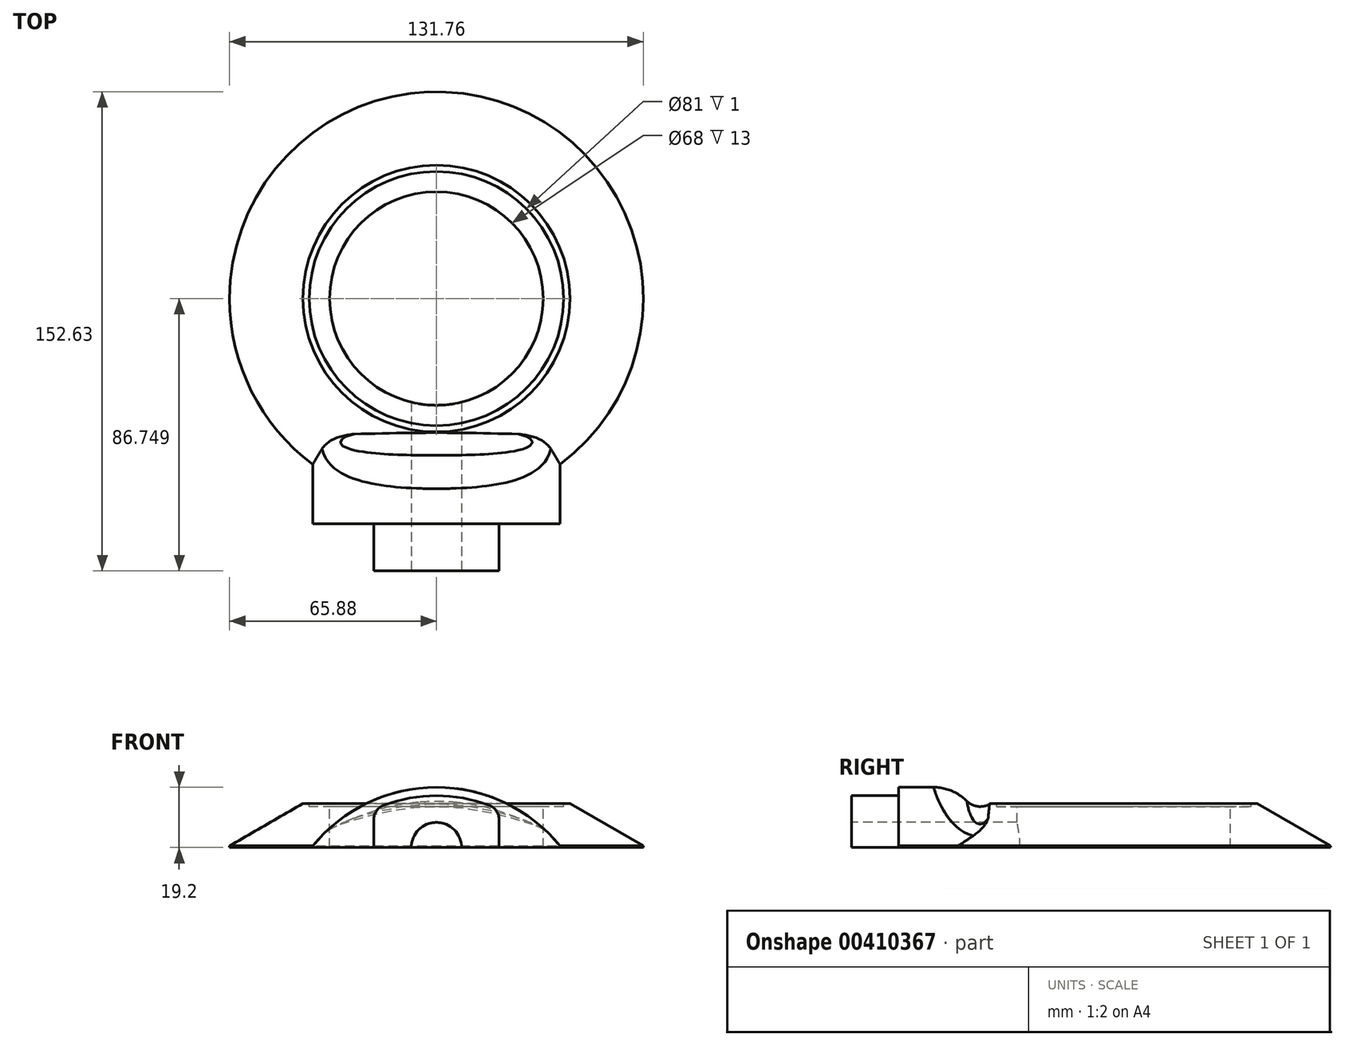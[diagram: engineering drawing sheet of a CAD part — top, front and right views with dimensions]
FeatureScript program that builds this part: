
annotation { "Feature Type Name" : "Feature", "Feature Type Description" : "" }
export const myFeature = defineFeature(function(context is Context, id is Id, definition is map)
    precondition{}
    {
        {
            var Q0;
            Q0=qCreatedBy(makeId("Front.planeOp"),FACE);
            var sketch = newSketch(context, id + "F0", { "sketchPlane" : qUnion([Q0])});
            skLineSegment(sketch, "E0", {"start": v(-39.5, 0) * mm, "end": v(39.5, 0) * mm});
            skPoint(sketch, "E1", {"position": v(0, 19) * mm});
            skLineSegment(sketch, "E2", {"start": v(39.5, 0) * mm, "end": v(39.5, 0) * mm});
            skLineSegment(sketch, "E3.MirrorCS", {"start": v(-39.5, 0) * mm, "end": v(-39.5, 0) * mm});
            skArc(sketch, "E4", {"start": v(39.5, 0) * mm, "mid": v(0, 19) * mm, "end": v(-39.5, 0) * mm});
            skSolve(sketch);
        }
        {
            var Q0;
            Q0=qCreatedBy(makeId("Front.planeOp"),FACE);
            var sketch = newSketch(context, id + "F1", { "sketchPlane" : qUnion([Q0])});
            skLineSegment(sketch, "E5.0", {"start": v(-39.35, 0) * mm, "end": v(0, 0) * mm});
            skArc(sketch, "E6.0", {"start": v(0, 19.2) * mm, "mid": v(-21.79, 14.29) * mm, "end": v(-39.35, 0.5) * mm});
            skLineSegment(sketch, "E7", {"start": v(-39.35, 0.5) * mm, "end": v(-39.35, 0) * mm});
            skArc(sketch, "E8.MirrorCS", {"start": v(0, 19.2) * mm, "mid": v(21.79, 14.29) * mm, "end": v(39.35, 0.5) * mm});
            skLineSegment(sketch, "E9.MirrorCS", {"start": v(39.35, 0.5) * mm, "end": v(39.35, 0) * mm});
            skLineSegment(sketch, "E10.MirrorCS", {"start": v(39.35, 0) * mm, "end": v(0, 0) * mm});
            skSolve(sketch);
        }
        {
            var Q0;
            Q0=qCreatedBy(makeId("Front.planeOp"),FACE);
            var sketch = newSketch(context, id + "F2", { "sketchPlane" : qUnion([Q0])});
            skArc(sketch, "E11.0", {"start": v(20, 12.14) * mm, "mid": v(0, 16.5) * mm, "end": v(-20, 12.14) * mm});
            skLineSegment(sketch, "E12", {"start": v(-20, 0) * mm, "end": v(20, 0) * mm});
            skLineSegment(sketch, "E13", {"start": v(20, 0) * mm, "end": v(20, 12.14) * mm});
            skLineSegment(sketch, "E14.MirrorCS", {"start": v(-20, 0) * mm, "end": v(-20, 12.14) * mm});
            skPoint(sketch, "E15.orphan", {"position": v(-36.25, 0) * mm});
            skSolve(sketch);
        }
        {
            var Q0;
            Q0=qCreatedBy(makeId("Right.planeOp"),FACE);
            var sketch = newSketch(context, id + "F3", { "sketchPlane" : qUnion([Q0])});
            skLineSegment(sketch, "E16", {"start": v(138.5, 0) * mm, "end": v(71.75, 0) * mm, "construction": true});
            skLineSegment(sketch, "E17", {"start": v(5.87, 0.5) * mm, "end": v(29.25, 14) * mm});
            skLineSegment(sketch, "E18", {"start": v(29.25, 14) * mm, "end": v(71.75, 14) * mm});
            skLineSegment(sketch, "E19", {"start": v(114.25, 14) * mm, "end": v(138.5, 0) * mm, "construction": true});
            skLineSegment(sketch, "E20", {"start": v(71.75, 0) * mm, "end": v(71.75, 41.66) * mm, "construction": true});
            skLineSegment(sketch, "E21", {"start": v(71.75, 14) * mm, "end": v(71.75, 0) * mm});
            skLineSegment(sketch, "E22", {"start": v(71.75, 14) * mm, "end": v(114.25, 14) * mm, "construction": true});
            skLineSegment(sketch, "E23", {"start": v(71.75, 0) * mm, "end": v(5.87, 0) * mm});
            skLineSegment(sketch, "E24", {"start": v(5.87, 0.5) * mm, "end": v(5.87, 0) * mm});
            skPoint(sketch, "E25.orphan", {"position": v(5, 0) * mm});
            skSolve(sketch);
        }
        {
            var Q0;
            Q0 = qSketchRegion(id + "F3", true);
            var Q1;
            Q1=sQuery(id+"F3.wireOp",EDGE,"E20");
            revolve(context, id + "F4", {"entities" : qUnion([Q0]), "axis" : qUnion([Q1]), "revolveType" : RevolveType.FULL});
        }
        {
            var Q0;
            Q0 = qSketchRegion(id + "F1", true);
            extrude(context, id + "F5", {"entities" : qUnion([Q0]), "operationType" : NewBodyOperationType.ADD, "oppositeDirection" : true, "depth" : 20 * mm});
        }
        {
            var Q0;
            Q0=makeQuery(id+"F4.opRevolve","SWEPT_FACE",FACE,{"disambiguationData":[OSD([sQuery(id+"F3.wireOp",EDGE,"E18")])]});
            var sketch = newSketch(context, id + "F6", { "sketchPlane" : qUnion([Q0])});
            skCircle(sketch, "E26", {"center": v(0, 71.75) * mm, "radius": 40.5 * mm});
            skSolve(sketch);
        }
        {
            var Q0;
            Q0 = qSketchRegion(id + "F6", true);
            extrude(context, id + "F7", {"entities" : qUnion([Q0]), "operationType" : NewBodyOperationType.REMOVE, "oppositeDirection" : true, "depth" : 1 * mm});
        }
        {
            var Q0;
            Q0 = qSketchRegion(id + "F2", true);
            extrude(context, id + "F8", {"entities" : qUnion([Q0]), "operationType" : NewBodyOperationType.ADD, "depth" : 15 * mm});
        }
        {
            var Q0;
            Q0=makeQuery(id+"F7.boolean.opBoolean","COPY",FACE,{"derivedFrom":makeQuery(id+"F7.opExtrude","CAP_FACE",FACE,{"disambiguationData":[OSD([sQuery(id+"F6.wireOp",EDGE,"E26")])],"isStart":false})});
            var sketch = newSketch(context, id + "F9", { "sketchPlane" : qUnion([Q0])});
            skCircle(sketch, "E27", {"center": v(0, 71.75) * mm, "radius": 34 * mm});
            skSolve(sketch);
        }
        {
            var Q0;
            Q0 = qSketchRegion(id + "F9", true);
            extrude(context, id + "F10", {"entities" : qUnion([Q0]), "operationType" : NewBodyOperationType.REMOVE, "endBound" : BoundingType.THROUGH_ALL, "oppositeDirection" : true, "depth" : 25 * mm});
        }
        {
            var Q0;
            Q0=makeQuery(id+"F8.opExtrude","SWEPT_EDGE",EDGE,{"disambiguationData":[OSD([sQuery(id+"F2.wireOp",EDGE,"E11.0"),sQuery(id+"F2.wireOp",EDGE,"E13")])]});
            var Q1;
            Q1=makeQuery(id+"F8.opExtrude","SWEPT_EDGE",EDGE,{"disambiguationData":[OSD([sQuery(id+"F2.wireOp",EDGE,"E11.0"),sQuery(id+"F2.wireOp",EDGE,"E14.MirrorCS")])]});
            fillet(context, id + "F11", {"entities" : qUnion([Q0, Q1]), "radius" : 5 * mm, "tangentPropagation" : true, "allowEdgeOverflow" : false});
        }
        {
            var Q0;
            Q0=qCreatedBy(makeId("Front.planeOp"),FACE);
            var sketch = newSketch(context, id + "F12", { "sketchPlane" : qUnion([Q0])});
            skCircle(sketch, "E28", {"center": v(0, 0) * mm, "radius": 8 * mm});
            skSolve(sketch);
        }
        {
            var Q0;
            Q0=makeQuery(id+"F12.imprint","IMPRINT",FACE,{"disambiguationData":[TD([[makeQuery(id+"F12.imprint","IMPRINT",EDGE,{"derivedFrom":sQuery(id+"F12.wireOp",EDGE,"E28")}),1.0]])]});
            extrude(context, id + "F13", {"entities" : qUnion([Q0]), "operationType" : NewBodyOperationType.REMOVE, "oppositeDirection" : true, "depth" : 70 * mm, "hasSecondDirection" : true, "secondDirectionOppositeDirection" : false, "secondDirectionDepth" : 25 * mm});
        }
        {
            var Q0;
            Q0=makeQuery(id+"F5.boolean.opBoolean","INTERSECT",EDGE,{"derivedFrom":[makeQuery(id+"F4.opRevolve","SWEPT_FACE",FACE,{"disambiguationData":[OSD([sQuery(id+"F3.wireOp",EDGE,"E17")])]}),makeQuery(id+"F5.opExtrude","CAP_FACE",FACE,{"disambiguationData":[OSD([sQuery(id+"F1.wireOp",EDGE,"E5.0"),sQuery(id+"F1.wireOp",EDGE,"E6.0"),sQuery(id+"F1.wireOp",EDGE,"E7"),sQuery(id+"F1.wireOp",EDGE,"E8.MirrorCS"),sQuery(id+"F1.wireOp",EDGE,"E9.MirrorCS"),sQuery(id+"F1.wireOp",EDGE,"E10.MirrorCS")])],"isStart":false})]});
            fillet(context, id + "F14", {"entities" : qUnion([Q0]), "radius" : 6 * mm, "tangentPropagation" : true, "allowEdgeOverflow" : false});
        }
        {
            var Q0;
            Q0=makeQuery(id+"F5.opExtrude","CAP_EDGE",EDGE,{"disambiguationData":[OSD([sQuery(id+"F1.wireOp",EDGE,"E6.0"),sQuery(id+"F1.wireOp",EDGE,"E8.MirrorCS")])],"isStart":false});
            fillet(context, id + "F15", {"entities" : qUnion([Q0]), "radius" : 15 * mm, "tangentPropagation" : true, "allowEdgeOverflow" : false});
        }
    });
